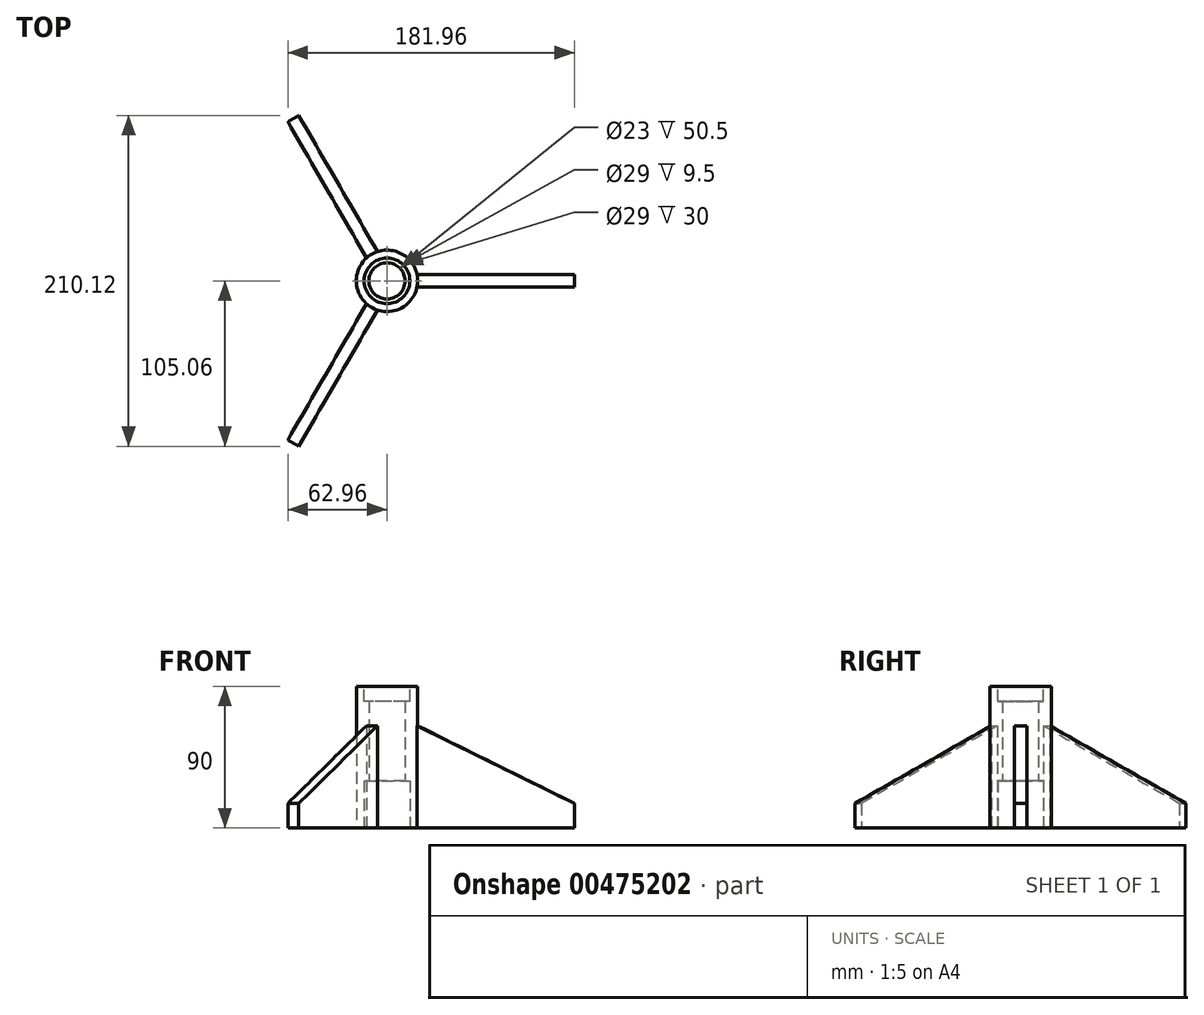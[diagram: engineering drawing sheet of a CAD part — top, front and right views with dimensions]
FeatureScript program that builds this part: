
annotation { "Feature Type Name" : "Feature", "Feature Type Description" : "" }
export const myFeature = defineFeature(function(context is Context, id is Id, definition is map)
    precondition{}
    {
        {
            var Q0;
            Q0=qCreatedBy(makeId("Top.planeOp"),FACE);
            var sketch = newSketch(context, id + "F0", { "sketchPlane" : qUnion([Q0])});
            skCircle(sketch, "E0", {"center": v(0, 0) * mm, "radius": 19.5 * mm});
            skCircle(sketch, "E1", {"center": v(0, 0) * mm, "radius": 11.5 * mm});
            skSolve(sketch);
        }
        {
            var Q0;
            Q0=makeQuery(id+"F0.imprint","IMPRINT",FACE,{"disambiguationData":[TD([[makeQuery(id+"F0.imprint","IMPRINT",EDGE,{"derivedFrom":sQuery(id+"F0.wireOp",EDGE,"E0")}),1.0]])]});
            extrude(context, id + "F1", {"entities" : qUnion([Q0]), "endBound" : BoundingType.SYMMETRIC, "depth" : 90 * mm});
        }
        {
            var Q0;
            Q0=makeQuery(id+"F1.opExtrude","CAP_FACE",FACE,{"disambiguationData":[OSD([sQuery(id+"F0.wireOp",EDGE,"E0"),sQuery(id+"F0.wireOp",EDGE,"E1")])],"isStart":false});
            var sketch = newSketch(context, id + "F2", { "sketchPlane" : qUnion([Q0])});
            skCircle(sketch, "E2", {"center": v(0, 0) * mm, "radius": 14.5 * mm});
            skCircle(sketch, "E3.0", {"center": v(0, 0) * mm, "radius": 11.5 * mm});
            skSolve(sketch);
        }
        {
            var Q0;
            Q0=makeQuery(id+"F2.imprint","IMPRINT",FACE,{"disambiguationData":[TD([[makeQuery(id+"F2.imprint","IMPRINT",EDGE,{"derivedFrom":sQuery(id+"F2.wireOp",EDGE,"E2")}),1.0]])]});
            extrude(context, id + "F3", {"entities" : qUnion([Q0]), "operationType" : NewBodyOperationType.REMOVE, "oppositeDirection" : true, "depth" : 9.5 * mm});
        }
        {
            var Q0;
            Q0=makeQuery(id+"F1.opExtrude","CAP_FACE",FACE,{"disambiguationData":[OSD([sQuery(id+"F0.wireOp",EDGE,"E0"),sQuery(id+"F0.wireOp",EDGE,"E1")])],"isStart":true});
            var sketch = newSketch(context, id + "F4", { "sketchPlane" : qUnion([Q0])});
            skCircle(sketch, "E4", {"center": v(0, 0) * mm, "radius": 14.5 * mm});
            skCircle(sketch, "E5.0", {"center": v(0, 0) * mm, "radius": 11.5 * mm});
            skSolve(sketch);
        }
        {
            var Q0;
            Q0=makeQuery(id+"F4.imprint","IMPRINT",FACE,{"disambiguationData":[TD([[makeQuery(id+"F4.imprint","IMPRINT",EDGE,{"derivedFrom":sQuery(id+"F4.wireOp",EDGE,"E4")}),1.0]])]});
            extrude(context, id + "F5", {"entities" : qUnion([Q0]), "operationType" : NewBodyOperationType.REMOVE, "oppositeDirection" : true, "depth" : 30 * mm});
        }
        {
            var Q0;
            Q0=qCreatedBy(makeId("Right.planeOp"),FACE);
            cPlane(context, id + "F6", {"entities" : qUnion([Q0]), "cplaneType" : CPlaneType.OFFSET, "offset" : 19 * mm, "width" : 150 * mm, "height" : 150 * mm});
        }
        {
            var Q0;
            Q0=qCreatedBy(id+"F6.planeOp",FACE);
            var sketch = newSketch(context, id + "F7", { "sketchPlane" : qUnion([Q0])});
            skLineSegment(sketch, "E6", {"start": v(-4, 20) * mm, "end": v(4, 20) * mm});
            skLineSegment(sketch, "E7", {"start": v(-4, 20) * mm, "end": v(-4, -45) * mm});
            skLineSegment(sketch, "E8", {"start": v(-4, -45) * mm, "end": v(4, -45) * mm});
            skLineSegment(sketch, "E9", {"start": v(4, -45) * mm, "end": v(4, 20) * mm});
            skSolve(sketch);
        }
        {
            var Q0;
            Q0=qCreatedBy(makeId("Right.planeOp"),FACE);
            var sketch = newSketch(context, id + "F8", { "sketchPlane" : qUnion([Q0])});
            skLineSegment(sketch, "E10", {"start": v(0, 61.67) * mm, "end": v(0, -54.72) * mm, "construction": true});
            skSolve(sketch);
        }
        {
            var Q0;
            Q0=qCreatedBy(makeId("Right.planeOp"),FACE);
            var Q1;
            Q1=sQuery(id+"F8.wireOp",EDGE,"E10");
            cPlane(context, id + "F9", {"entities" : qUnion([Q0, Q1]), "cplaneType" : CPlaneType.LINE_ANGLE, "offset" : 25 * mm, "angle" : 120 * degree, "width" : 150 * mm, "height" : 150 * mm});
        }
        {
            var Q0;
            Q0=makeQuery(id+"FmNTNJQfuQ9f8jD_1.boolean.opBoolean","MERGE",FACE,{"derivedFrom":[makeQuery(id+"F1.opExtrude","CAP_FACE",FACE,{"disambiguationData":[OSD([sQuery(id+"F0.wireOp",EDGE,"E0"),sQuery(id+"F0.wireOp",EDGE,"E1")])],"isStart":true}),makeQuery(id+"FmNTNJQfuQ9f8jD_1.opExtrude","SWEPT_FACE",FACE,{"disambiguationData":[OSD([sQuery(id+"F7.wireOp",EDGE,"E8")])]})]});
            var sketch = newSketch(context, id + "F10", { "sketchPlane" : qUnion([Q0])});
            skLineSegment(sketch, "E11.0", {"start": v(119, 4) * mm, "end": v(19.09, 4) * mm});
            skLineSegment(sketch, "E12.0", {"start": v(119, 4) * mm, "end": v(119, -4) * mm});
            skLineSegment(sketch, "E13.0", {"start": v(119, -4) * mm, "end": v(19.09, -4) * mm});
            skLineSegment(sketch, "E14", {"start": v(19.09, 4) * mm, "end": v(19.09, -4) * mm});
            skLineSegment(sketch, "E15.1.0", {"start": v(-62.96, 101.06) * mm, "end": v(-13, 14.53) * mm});
            skLineSegment(sketch, "E15.1.1", {"start": v(-56.04, 105.06) * mm, "end": v(-6.08, 18.53) * mm});
            skLineSegment(sketch, "E15.1.2", {"start": v(-62.96, 101.06) * mm, "end": v(-56.04, 105.06) * mm});
            skLineSegment(sketch, "E15.1.3", {"start": v(-13, 14.53) * mm, "end": v(-6.08, 18.53) * mm});
            skLineSegment(sketch, "E15.2.0", {"start": v(-56.04, -105.06) * mm, "end": v(-6.08, -18.53) * mm});
            skLineSegment(sketch, "E15.2.1", {"start": v(-62.96, -101.06) * mm, "end": v(-13, -14.53) * mm});
            skLineSegment(sketch, "E15.2.2", {"start": v(-56.04, -105.06) * mm, "end": v(-62.96, -101.06) * mm});
            skLineSegment(sketch, "E15.2.3", {"start": v(-6.08, -18.53) * mm, "end": v(-13, -14.53) * mm});
            skPoint(sketch, "E15.center", {"position": v(0, 0) * mm});
            skSolve(sketch);
        }
        {
            var Q0;
            Q0 = qSketchRegion(id + "F10", true);
            extrude(context, id + "F11", {"entities" : qUnion([Q0]), "operationType" : NewBodyOperationType.ADD, "oppositeDirection" : true, "depth" : 65 * mm});
        }
        {
            var Q0;
            Q0=makeQuery(id+"F11.opExtrude","SWEPT_FACE",FACE,{"disambiguationData":[OSD([sQuery(id+"F10.wireOp",EDGE,"E11.0")])]});
            var sketch = newSketch(context, id + "F12", { "sketchPlane" : qUnion([Q0])});
            skLineSegment(sketch, "E16", {"start": v(19.09, 20) * mm, "end": v(119, -29.38) * mm});
            skLineSegment(sketch, "E17", {"start": v(119, -29.38) * mm, "end": v(119, 20) * mm});
            skLineSegment(sketch, "E18", {"start": v(119, 20) * mm, "end": v(19.09, 20) * mm});
            skSolve(sketch);
        }
        {
            var Q0;
            Q0=makeQuery(id+"F12.imprint","IMPRINT",FACE,{"disambiguationData":[TD([[makeQuery(id+"F12.imprint","IMPRINT",EDGE,{"derivedFrom":sQuery(id+"F12.wireOp",EDGE,"E16")}),1.0]])]});
            var Q1;
            Q1=sQuery(id+"F8.wireOp",EDGE,"E10");
            revolve(context, id + "F13", {"operationType" : NewBodyOperationType.REMOVE, "entities" : qUnion([Q0]), "axis" : qUnion([Q1]), "revolveType" : RevolveType.FULL, "oppositeDirection" : true});
        }
    });
